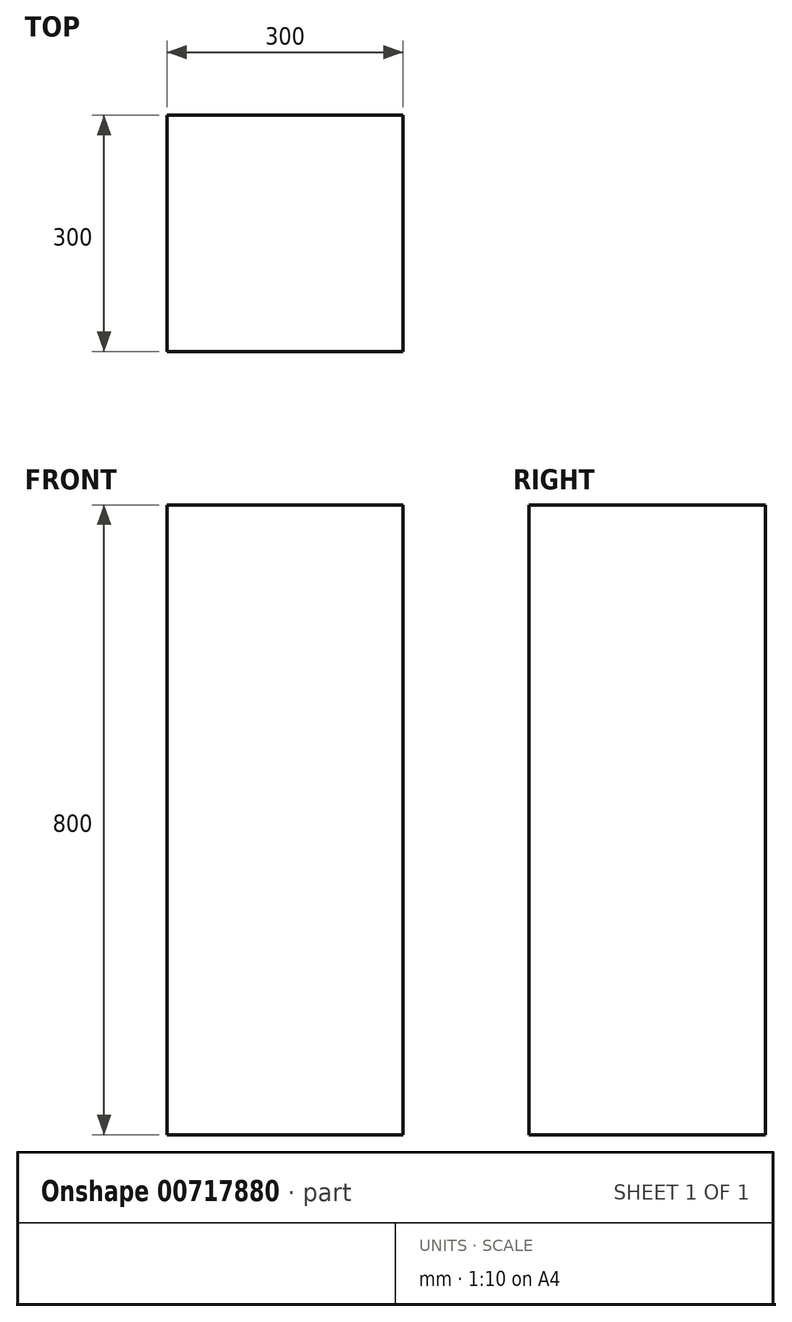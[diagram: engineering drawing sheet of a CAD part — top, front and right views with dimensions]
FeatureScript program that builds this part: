
annotation { "Feature Type Name" : "Feature", "Feature Type Description" : "" }
export const myFeature = defineFeature(function(context is Context, id is Id, definition is map)
    precondition{}
    {
        {
            var Q0;
            Q0=qCreatedBy(makeId("Top.planeOp"),FACE);
            var sketch = newSketch(context, id + "F0", { "sketchPlane" : qUnion([Q0])});
            skLineSegment(sketch, "E0.bottom", {"start": v(-161.17, 179.08) * mm, "end": v(138.83, 179.08) * mm});
            skLineSegment(sketch, "E0.top", {"start": v(-161.17, -120.92) * mm, "end": v(138.83, -120.92) * mm});
            skLineSegment(sketch, "E0.left", {"start": v(-161.17, 179.08) * mm, "end": v(-161.17, -120.92) * mm});
            skLineSegment(sketch, "E0.right", {"start": v(138.83, 179.08) * mm, "end": v(138.83, -120.92) * mm});
            skSolve(sketch);
        }
        {
            var Q0;
            Q0=makeQuery(id+"F0.imprint","IMPRINT",FACE,{"disambiguationData":[TD([[makeQuery(id+"F0.imprint","IMPRINT",EDGE,{"derivedFrom":sQuery(id+"F0.wireOp",EDGE,"E0.bottom")}),-1.0]])]});
            extrude(context, id + "F1", {"entities" : qUnion([Q0]), "depth" : 800 * mm, "offsetDistance" : 25 * mm});
        }
    });
